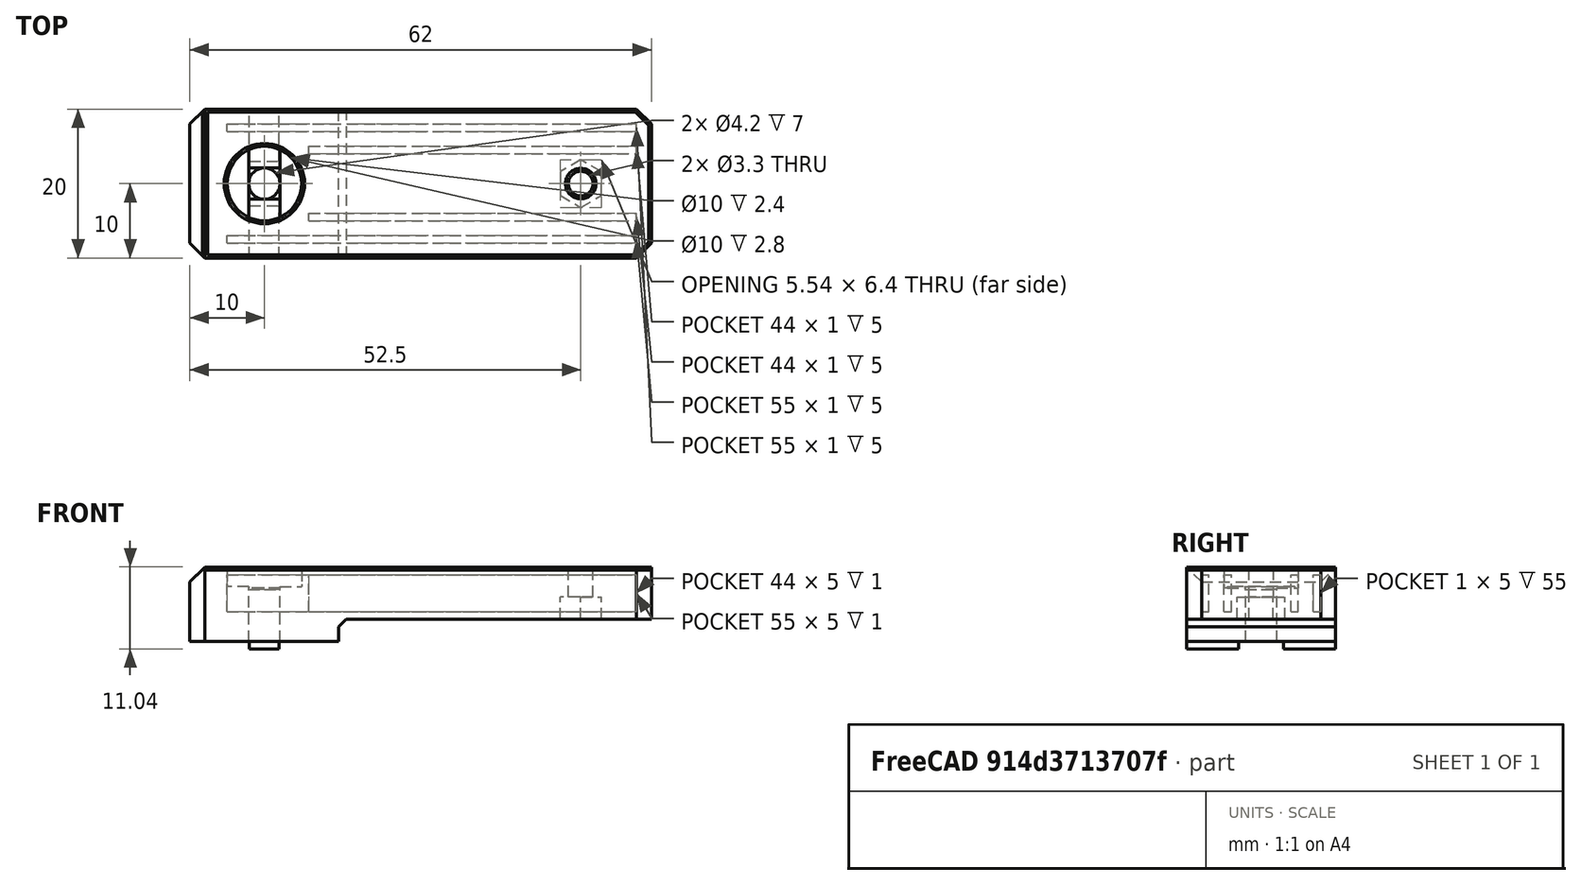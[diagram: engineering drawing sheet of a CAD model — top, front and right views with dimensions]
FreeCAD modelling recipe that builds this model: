
FCSTD DOCUMENT  (FreeCAD 0.18R14555 (Git shallow))
Label: filament-dryer.-plate-cooler-mountFCStd
License: All rights reserved
LicenseURL: http://en.wikipedia.org/wiki/All_rights_reserved
objects: Part::Box×8, Part::Cut×5, Part::MultiFuse×3, Part::Feature×3, Part::Chamfer×3, Part::Cylinder×2
note: 24 computed .brp shape members not serialized (recipe doc carries the construction recipe); baked Part::Feature solids carry a one-line shape summary decoded from their .brp

FEATURE [Part::Box] Box  label="Cube"
  AttacherType = Attacher::AttachEngine3D
  Height = 10
  Length = 20
  Width = 20
FEATURE [Part::Box] Box001  label="Cube001"
  AttacherType = Attacher::AttachEngine3D
  Height = 7
  Length = 52
  Placement = pos=(10,0,3) rot=(0,0,1;0rad)
  Width = 20
FEATURE [Part::MultiFuse] Fusion
  Shapes = -> [Box,Box001]
FEATURE [Part::Feature] Body001  label="nut-slot"
  Placement = pos=(52.5,10,3) rot=(0,0,1;0rad)
  shape: bbox 5.543 x 6.4 x 3 mm, 8 faces (baked)
FEATURE [Part::Cut] Cut
  Base = -> Fusion
  Tool = -> Body001
FEATURE [Part::Chamfer] Chamfer
  Base = -> Cut
  Edges = 5 edges r=2: [Edge1,Edge2,Edge3,Edge32,Edge36]
FEATURE [Part::Cylinder] Cylinder
  Angle = 360
  AttacherType = Attacher::AttachEngine3D
  Height = 10
  Placement = pos=(52.5,10,0) rot=(0,0,1;0rad)
  Radius = 1.65
FEATURE [Part::Cut] Cut001
  Base = -> Chamfer
  Tool = -> Cylinder
FEATURE [Part::Chamfer] Chamfer001
  Base = -> Cut001
  Edges = 1 edges r=1: [Edge23]
FEATURE [Part::Cylinder] Cylinder001
  Angle = 360
  AttacherType = Attacher::AttachEngine3D
  Height = 10
  Placement = pos=(10,10,0) rot=(0,0,1;0rad)
  Radius = 2.1
FEATURE [Part::Cut] Cut002
  Base = -> Chamfer001
  Tool = -> Cylinder001
FEATURE [Part::Feature] Cut003012  label="screw-template006"
  Placement = pos=(20,0,9) rot=(0,1,0;3.14159rad)
  shape: bbox 10 x 10 x 7 mm, 11 faces (baked)
FEATURE [Part::Cut] Cut003013
  Base = -> Cut002
  Tool = -> Cut003012
FEATURE [Part::Feature] Cut003013001  label="Cut003014"
  shape: bbox 62 x 20 x 10 mm, 36 faces (baked)
FEATURE [Part::Chamfer] Chamfer002
  Base = -> Cut003013001
  Edges = 10 edges r=0.4: [Edge30,Edge40,Edge43,Edge44,Edge67,Edge68,Edge69,Edge70,Edge71,Edge72]
FEATURE [Part::Box] Box002  label="Cube002"
  AttacherType = Attacher::AttachEngine3D
  Height = 5
  Length = 55
  Placement = pos=(5,2,4) rot=(0,0,1;0rad)
  Width = 1
FEATURE [Part::Box] Box003  label="Cube003"
  AttacherType = Attacher::AttachEngine3D
  Height = 5
  Length = 55
  Placement = pos=(5,17,4) rot=(0,0,1;0rad)
  Width = 1
FEATURE [Part::Box] Box004  label="Cube004"
  AttacherType = Attacher::AttachEngine3D
  Height = 5
  Length = 44
  Placement = pos=(16,5,4) rot=(0,0,1;0rad)
  Width = 1
FEATURE [Part::Box] Box005  label="Cube005"
  AttacherType = Attacher::AttachEngine3D
  Height = 5
  Length = 44
  Placement = pos=(16,14,4) rot=(0,0,1;0rad)
  Width = 1
FEATURE [Part::MultiFuse] Fusion001
  Shapes = -> [Box005,Box002,Box004,Box003]
FEATURE [Part::Cut] Cut003013002
  Base = -> Chamfer002
  Tool = -> Fusion001
FEATURE [Part::Box] Box006  label="Cube006"
  AttacherType = Attacher::AttachEngine3D
  Height = 1
  Length = 4
  Placement = pos=(8,0,-1) rot=(0,0,1;0rad)
  Width = 7
FEATURE [Part::Box] Box007  label="Cube007"
  AttacherType = Attacher::AttachEngine3D
  Height = 1
  Length = 4
  Placement = pos=(8,13,-1) rot=(0,0,1;0rad)
  Width = 7
FEATURE [Part::MultiFuse] Fusion002
  Shapes = -> [Cut003013002,Box006,Box007]
